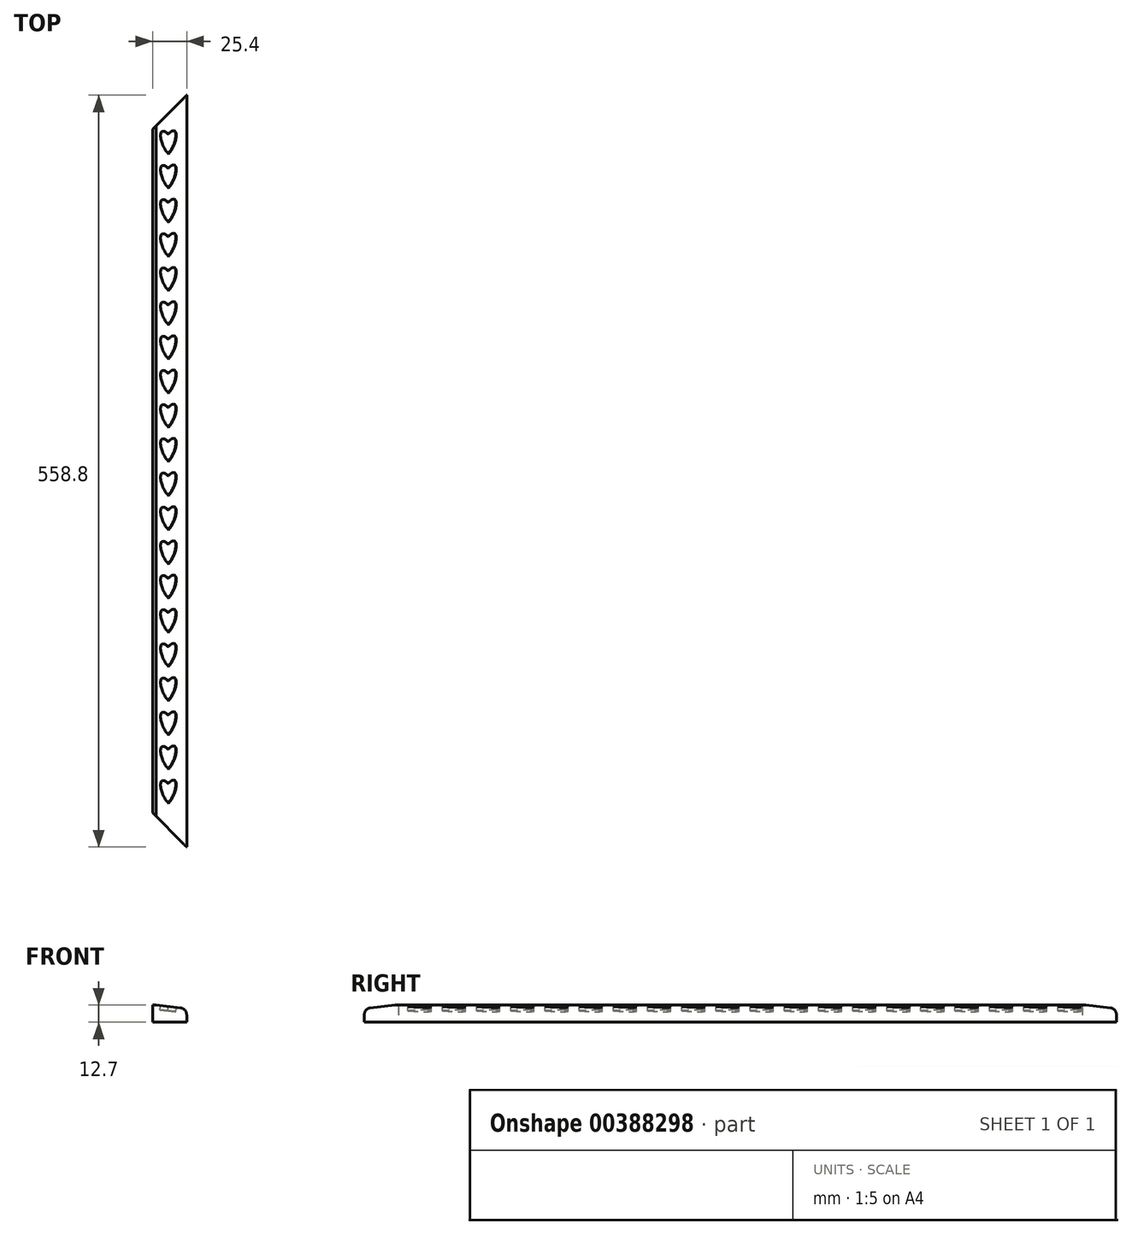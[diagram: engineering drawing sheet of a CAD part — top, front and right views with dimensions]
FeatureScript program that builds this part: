
annotation { "Feature Type Name" : "Feature", "Feature Type Description" : "" }
export const myFeature = defineFeature(function(context is Context, id is Id, definition is map)
    precondition{}
    {
        {
            var Q0;
            Q0=qCreatedBy(makeId("Top.planeOp"),FACE);
            var sketch = newSketch(context, id + "F0", { "sketchPlane" : qUnion([Q0])});
            skLineSegment(sketch, "E0.bottom", {"start": v(-12.7, 279.4) * mm, "end": v(12.7, 279.4) * mm});
            skLineSegment(sketch, "E0.top", {"start": v(-12.7, -279.4) * mm, "end": v(12.7, -279.4) * mm});
            skLineSegment(sketch, "E0.left", {"start": v(-12.7, 279.4) * mm, "end": v(-12.7, -279.4) * mm});
            skLineSegment(sketch, "E0.right", {"start": v(12.7, 279.4) * mm, "end": v(12.7, -279.4) * mm});
            skPoint(sketch, "E0.middle", {"position": v(0, 0) * mm});
            skPoint(sketch, "E1.end.orphan", {"position": v(12.7, -254) * mm});
            skPoint(sketch, "E2.MirrorCS.end.orphan", {"position": v(12.7, 254) * mm});
            skPoint(sketch, "E2.MirrorCS.start.orphan", {"position": v(-12.7, 279.4) * mm});
            skLineSegment(sketch, "E3", {"start": v(12.7, 279.4) * mm, "end": v(-12.7, 254) * mm});
            skLineSegment(sketch, "E4.MirrorCS", {"start": v(12.7, -279.4) * mm, "end": v(-12.7, -254) * mm});
            skSolve(sketch);
        }
        {
            var Q0;
            Q0=makeQuery(id+"F0.imprint","IMPRINT",FACE,{"disambiguationData":[TD([[makeQuery(id+"F0.imprint","IMPRINT",EDGE,{"derivedFrom":sQuery(id+"F0.wireOp",EDGE,"E0.right")}),-1.0]])]});
            extrude(context, id + "F1", {"entities" : qUnion([Q0]), "depth" : 12.7 * mm});
        }
        {
            var Q0;
            Q0=makeQuery(id+"F1.opExtrude","CAP_EDGE",EDGE,{"disambiguationData":[OSD([sQuery(id+"F0.wireOp",EDGE,"E0.right")])],"isStart":false});
            chamfer(context, id + "F2", {"entities" : qUnion([Q0]), "chamferType" : ChamferType.TWO_OFFSETS, "width1" : 2.54 * mm, "oppositeDirection" : false, "width2" : 22.86 * mm, "tangentPropagation" : true});
        }
        {
            var Q0;
            {var subQ0=sQuery(id+"F0.wireOp",EDGE,"E0.right");Q0=makeQuery(id+"F2.opChamfer","BLEND_EDGE",EDGE,{"blendedFrom":[makeQuery(id+"F1.opExtrude","CAP_EDGE",EDGE,{"disambiguationData":[OSD([subQ0])],"isStart":false}),makeQuery(id+"F1.opExtrude","SWEPT_FACE",FACE,{"disambiguationData":[OSD([subQ0])]})],"blendedInto":[makeQuery(id+"F1.opExtrude","SWEPT_FACE",FACE,{"disambiguationData":[OSD([subQ0])]})]});}
            fillet(context, id + "F3", {"entities" : qUnion([Q0]), "radius" : 5.08 * mm, "tangentPropagation" : true, "allowEdgeOverflow" : false});
        }
        {
            var Q0;
            Q0=makeQuery(id+"F2.opChamfer","BLEND_FACE",FACE,{"disambiguationData":[OSD([sQuery(id+"F0.wireOp",EDGE,"E0.right")])]});
            var sketch = newSketch(context, id + "F4", { "sketchPlane" : qUnion([Q0])});
            skLineSegment(sketch, "E5.bottom", {"start": v(-8.83, 253.3) * mm, "end": v(4.54, 253.3) * mm});
            skLineSegment(sketch, "E5.top", {"start": v(-8.83, 232.97) * mm, "end": v(4.54, 232.97) * mm});
            skLineSegment(sketch, "E5.left", {"start": v(-8.83, 253.3) * mm, "end": v(-8.83, 232.97) * mm});
            skLineSegment(sketch, "E5.right", {"start": v(4.54, 253.3) * mm, "end": v(4.54, 232.97) * mm});
            skEllipticalArc(sketch, "E6", {});
            skPoint(sketch, "E6.centerSnap0", {"position": v(-8.83, 243.13) * mm});
            skPoint(sketch, "E6.centerSnap1", {"position": v(-2.15, 232.97) * mm});
            skEllipticalArc(sketch, "E7", {});
            skLineSegment(sketch, "E8", {"start": v(-2.22, 250.5) * mm, "end": v(-1.95, 250.22) * mm});
            skPoint(sketch, "E9.left.start.orphan", {"position": v(-11.37, 255.83) * mm});
            skLineSegment(sketch, "E10.0.1.0", {"start": v(-8.83, 227.9) * mm, "end": v(4.54, 227.9) * mm});
            skPoint(sketch, "E10.0.1.1", {"position": v(-2.15, 207.57) * mm});
            skLineSegment(sketch, "E10.0.1.2", {"start": v(-8.83, 227.9) * mm, "end": v(-8.83, 207.57) * mm});
            skPoint(sketch, "E10.0.1.3", {"position": v(-11.37, 230.43) * mm});
            skLineSegment(sketch, "E10.0.1.4", {"start": v(4.54, 227.9) * mm, "end": v(4.54, 207.57) * mm});
            skPoint(sketch, "E10.0.1.5", {"position": v(-8.83, 217.73) * mm});
            skEllipticalArc(sketch, "E10.0.1.6", {});
            skEllipticalArc(sketch, "E10.0.1.7", {});
            skLineSegment(sketch, "E10.0.1.8", {"start": v(-8.83, 207.57) * mm, "end": v(4.54, 207.57) * mm});
            skLineSegment(sketch, "E10.0.1.9", {"start": v(-2.22, 225.1) * mm, "end": v(-1.95, 224.82) * mm});
            skLineSegment(sketch, "E10.0.2.0", {"start": v(-8.83, 202.5) * mm, "end": v(4.54, 202.5) * mm});
            skPoint(sketch, "E10.0.2.1", {"position": v(-2.15, 182.17) * mm});
            skLineSegment(sketch, "E10.0.2.2", {"start": v(-8.83, 202.5) * mm, "end": v(-8.83, 182.17) * mm});
            skPoint(sketch, "E10.0.2.3", {"position": v(-11.37, 205.03) * mm});
            skLineSegment(sketch, "E10.0.2.4", {"start": v(4.54, 202.5) * mm, "end": v(4.54, 182.17) * mm});
            skPoint(sketch, "E10.0.2.5", {"position": v(-8.83, 192.33) * mm});
            skEllipticalArc(sketch, "E10.0.2.6", {});
            skEllipticalArc(sketch, "E10.0.2.7", {});
            skLineSegment(sketch, "E10.0.2.8", {"start": v(-8.83, 182.17) * mm, "end": v(4.54, 182.17) * mm});
            skLineSegment(sketch, "E10.0.2.9", {"start": v(-2.22, 199.7) * mm, "end": v(-1.95, 199.42) * mm});
            skLineSegment(sketch, "E10.0.3.0", {"start": v(-8.83, 177.1) * mm, "end": v(4.54, 177.1) * mm});
            skPoint(sketch, "E10.0.3.1", {"position": v(-2.15, 156.77) * mm});
            skLineSegment(sketch, "E10.0.3.2", {"start": v(-8.83, 177.1) * mm, "end": v(-8.83, 156.77) * mm});
            skPoint(sketch, "E10.0.3.3", {"position": v(-11.37, 179.63) * mm});
            skLineSegment(sketch, "E10.0.3.4", {"start": v(4.54, 177.1) * mm, "end": v(4.54, 156.77) * mm});
            skPoint(sketch, "E10.0.3.5", {"position": v(-8.83, 166.93) * mm});
            skEllipticalArc(sketch, "E10.0.3.6", {});
            skEllipticalArc(sketch, "E10.0.3.7", {});
            skLineSegment(sketch, "E10.0.3.8", {"start": v(-8.83, 156.77) * mm, "end": v(4.54, 156.77) * mm});
            skLineSegment(sketch, "E10.0.3.9", {"start": v(-2.22, 174.3) * mm, "end": v(-1.95, 174.02) * mm});
            skLineSegment(sketch, "E10.0.4.0", {"start": v(-8.83, 151.7) * mm, "end": v(4.54, 151.7) * mm});
            skPoint(sketch, "E10.0.4.1", {"position": v(-2.15, 131.37) * mm});
            skLineSegment(sketch, "E10.0.4.2", {"start": v(-8.83, 151.7) * mm, "end": v(-8.83, 131.37) * mm});
            skPoint(sketch, "E10.0.4.3", {"position": v(-11.37, 154.23) * mm});
            skLineSegment(sketch, "E10.0.4.4", {"start": v(4.54, 151.7) * mm, "end": v(4.54, 131.37) * mm});
            skPoint(sketch, "E10.0.4.5", {"position": v(-8.83, 141.53) * mm});
            skEllipticalArc(sketch, "E10.0.4.6", {});
            skEllipticalArc(sketch, "E10.0.4.7", {});
            skLineSegment(sketch, "E10.0.4.8", {"start": v(-8.83, 131.37) * mm, "end": v(4.54, 131.37) * mm});
            skLineSegment(sketch, "E10.0.4.9", {"start": v(-2.22, 148.9) * mm, "end": v(-1.95, 148.62) * mm});
            skLineSegment(sketch, "E10.0.5.0", {"start": v(-8.83, 126.3) * mm, "end": v(4.54, 126.3) * mm});
            skPoint(sketch, "E10.0.5.1", {"position": v(-2.15, 105.97) * mm});
            skLineSegment(sketch, "E10.0.5.2", {"start": v(-8.83, 126.3) * mm, "end": v(-8.83, 105.97) * mm});
            skPoint(sketch, "E10.0.5.3", {"position": v(-11.37, 128.83) * mm});
            skLineSegment(sketch, "E10.0.5.4", {"start": v(4.54, 126.3) * mm, "end": v(4.54, 105.97) * mm});
            skPoint(sketch, "E10.0.5.5", {"position": v(-8.83, 116.13) * mm});
            skEllipticalArc(sketch, "E10.0.5.6", {});
            skEllipticalArc(sketch, "E10.0.5.7", {});
            skLineSegment(sketch, "E10.0.5.8", {"start": v(-8.83, 105.97) * mm, "end": v(4.54, 105.97) * mm});
            skLineSegment(sketch, "E10.0.5.9", {"start": v(-2.22, 123.5) * mm, "end": v(-1.95, 123.22) * mm});
            skLineSegment(sketch, "E10.0.6.0", {"start": v(-8.83, 100.9) * mm, "end": v(4.54, 100.9) * mm});
            skPoint(sketch, "E10.0.6.1", {"position": v(-2.15, 80.57) * mm});
            skLineSegment(sketch, "E10.0.6.2", {"start": v(-8.83, 100.9) * mm, "end": v(-8.83, 80.57) * mm});
            skPoint(sketch, "E10.0.6.3", {"position": v(-11.37, 103.43) * mm});
            skLineSegment(sketch, "E10.0.6.4", {"start": v(4.54, 100.9) * mm, "end": v(4.54, 80.57) * mm});
            skPoint(sketch, "E10.0.6.5", {"position": v(-8.83, 90.73) * mm});
            skEllipticalArc(sketch, "E10.0.6.6", {});
            skEllipticalArc(sketch, "E10.0.6.7", {});
            skLineSegment(sketch, "E10.0.6.8", {"start": v(-8.83, 80.57) * mm, "end": v(4.54, 80.57) * mm});
            skLineSegment(sketch, "E10.0.6.9", {"start": v(-2.22, 98.1) * mm, "end": v(-1.95, 97.82) * mm});
            skLineSegment(sketch, "E10.0.7.0", {"start": v(-8.83, 75.5) * mm, "end": v(4.54, 75.5) * mm});
            skPoint(sketch, "E10.0.7.1", {"position": v(-2.15, 55.17) * mm});
            skLineSegment(sketch, "E10.0.7.2", {"start": v(-8.83, 75.5) * mm, "end": v(-8.83, 55.17) * mm});
            skPoint(sketch, "E10.0.7.3", {"position": v(-11.37, 78.03) * mm});
            skLineSegment(sketch, "E10.0.7.4", {"start": v(4.54, 75.5) * mm, "end": v(4.54, 55.17) * mm});
            skPoint(sketch, "E10.0.7.5", {"position": v(-8.83, 65.33) * mm});
            skEllipticalArc(sketch, "E10.0.7.6", {});
            skEllipticalArc(sketch, "E10.0.7.7", {});
            skLineSegment(sketch, "E10.0.7.8", {"start": v(-8.83, 55.17) * mm, "end": v(4.54, 55.17) * mm});
            skLineSegment(sketch, "E10.0.7.9", {"start": v(-2.22, 72.7) * mm, "end": v(-1.95, 72.42) * mm});
            skLineSegment(sketch, "E10.0.8.0", {"start": v(-8.83, 50.1) * mm, "end": v(4.54, 50.1) * mm});
            skPoint(sketch, "E10.0.8.1", {"position": v(-2.15, 29.77) * mm});
            skLineSegment(sketch, "E10.0.8.2", {"start": v(-8.83, 50.1) * mm, "end": v(-8.83, 29.77) * mm});
            skPoint(sketch, "E10.0.8.3", {"position": v(-11.37, 52.63) * mm});
            skLineSegment(sketch, "E10.0.8.4", {"start": v(4.54, 50.1) * mm, "end": v(4.54, 29.77) * mm});
            skPoint(sketch, "E10.0.8.5", {"position": v(-8.83, 39.93) * mm});
            skEllipticalArc(sketch, "E10.0.8.6", {});
            skEllipticalArc(sketch, "E10.0.8.7", {});
            skLineSegment(sketch, "E10.0.8.8", {"start": v(-8.83, 29.77) * mm, "end": v(4.54, 29.77) * mm});
            skLineSegment(sketch, "E10.0.8.9", {"start": v(-2.22, 47.3) * mm, "end": v(-1.95, 47.02) * mm});
            skLineSegment(sketch, "E10.0.9.0", {"start": v(-8.83, 24.7) * mm, "end": v(4.54, 24.7) * mm});
            skPoint(sketch, "E10.0.9.1", {"position": v(-2.15, 4.37) * mm});
            skLineSegment(sketch, "E10.0.9.2", {"start": v(-8.83, 24.7) * mm, "end": v(-8.83, 4.37) * mm});
            skPoint(sketch, "E10.0.9.3", {"position": v(-11.37, 27.23) * mm});
            skLineSegment(sketch, "E10.0.9.4", {"start": v(4.54, 24.7) * mm, "end": v(4.54, 4.37) * mm});
            skPoint(sketch, "E10.0.9.5", {"position": v(-8.83, 14.53) * mm});
            skEllipticalArc(sketch, "E10.0.9.6", {});
            skEllipticalArc(sketch, "E10.0.9.7", {});
            skLineSegment(sketch, "E10.0.9.8", {"start": v(-8.83, 4.37) * mm, "end": v(4.54, 4.37) * mm});
            skLineSegment(sketch, "E10.0.9.9", {"start": v(-2.22, 21.9) * mm, "end": v(-1.95, 21.62) * mm});
            skLineSegment(sketch, "E10.0.10.0", {"start": v(-8.83, -0.7) * mm, "end": v(4.54, -0.7) * mm});
            skPoint(sketch, "E10.0.10.1", {"position": v(-2.15, -21.03) * mm});
            skLineSegment(sketch, "E10.0.10.2", {"start": v(-8.83, -0.7) * mm, "end": v(-8.83, -21.03) * mm});
            skPoint(sketch, "E10.0.10.3", {"position": v(-11.37, 1.83) * mm});
            skLineSegment(sketch, "E10.0.10.4", {"start": v(4.54, -0.7) * mm, "end": v(4.54, -21.03) * mm});
            skPoint(sketch, "E10.0.10.5", {"position": v(-8.83, -10.87) * mm});
            skEllipticalArc(sketch, "E10.0.10.6", {});
            skEllipticalArc(sketch, "E10.0.10.7", {});
            skLineSegment(sketch, "E10.0.10.8", {"start": v(-8.83, -21.03) * mm, "end": v(4.54, -21.03) * mm});
            skLineSegment(sketch, "E10.0.10.9", {"start": v(-2.22, -3.5) * mm, "end": v(-1.95, -3.78) * mm});
            skLineSegment(sketch, "E10.0.11.0", {"start": v(-8.83, -26.1) * mm, "end": v(4.54, -26.1) * mm});
            skPoint(sketch, "E10.0.11.1", {"position": v(-2.15, -46.43) * mm});
            skLineSegment(sketch, "E10.0.11.2", {"start": v(-8.83, -26.1) * mm, "end": v(-8.83, -46.43) * mm});
            skPoint(sketch, "E10.0.11.3", {"position": v(-11.37, -23.57) * mm});
            skLineSegment(sketch, "E10.0.11.4", {"start": v(4.54, -26.1) * mm, "end": v(4.54, -46.43) * mm});
            skPoint(sketch, "E10.0.11.5", {"position": v(-8.83, -36.27) * mm});
            skEllipticalArc(sketch, "E10.0.11.6", {});
            skEllipticalArc(sketch, "E10.0.11.7", {});
            skLineSegment(sketch, "E10.0.11.8", {"start": v(-8.83, -46.43) * mm, "end": v(4.54, -46.43) * mm});
            skLineSegment(sketch, "E10.0.11.9", {"start": v(-2.22, -28.9) * mm, "end": v(-1.95, -29.18) * mm});
            skLineSegment(sketch, "E10.0.12.0", {"start": v(-8.83, -51.5) * mm, "end": v(4.54, -51.5) * mm});
            skPoint(sketch, "E10.0.12.1", {"position": v(-2.15, -71.83) * mm});
            skLineSegment(sketch, "E10.0.12.2", {"start": v(-8.83, -51.5) * mm, "end": v(-8.83, -71.83) * mm});
            skPoint(sketch, "E10.0.12.3", {"position": v(-11.37, -48.97) * mm});
            skLineSegment(sketch, "E10.0.12.4", {"start": v(4.54, -51.5) * mm, "end": v(4.54, -71.83) * mm});
            skPoint(sketch, "E10.0.12.5", {"position": v(-8.83, -61.67) * mm});
            skEllipticalArc(sketch, "E10.0.12.6", {});
            skEllipticalArc(sketch, "E10.0.12.7", {});
            skLineSegment(sketch, "E10.0.12.8", {"start": v(-8.83, -71.83) * mm, "end": v(4.54, -71.83) * mm});
            skLineSegment(sketch, "E10.0.12.9", {"start": v(-2.22, -54.3) * mm, "end": v(-1.95, -54.58) * mm});
            skLineSegment(sketch, "E10.0.13.0", {"start": v(-8.83, -76.9) * mm, "end": v(4.54, -76.9) * mm});
            skPoint(sketch, "E10.0.13.1", {"position": v(-2.15, -97.23) * mm});
            skLineSegment(sketch, "E10.0.13.2", {"start": v(-8.83, -76.9) * mm, "end": v(-8.83, -97.23) * mm});
            skPoint(sketch, "E10.0.13.3", {"position": v(-11.37, -74.37) * mm});
            skLineSegment(sketch, "E10.0.13.4", {"start": v(4.54, -76.9) * mm, "end": v(4.54, -97.23) * mm});
            skPoint(sketch, "E10.0.13.5", {"position": v(-8.83, -87.07) * mm});
            skEllipticalArc(sketch, "E10.0.13.6", {});
            skEllipticalArc(sketch, "E10.0.13.7", {});
            skLineSegment(sketch, "E10.0.13.8", {"start": v(-8.83, -97.23) * mm, "end": v(4.54, -97.23) * mm});
            skLineSegment(sketch, "E10.0.13.9", {"start": v(-2.22, -79.7) * mm, "end": v(-1.95, -79.98) * mm});
            skLineSegment(sketch, "E10.0.14.0", {"start": v(-8.83, -102.3) * mm, "end": v(4.54, -102.3) * mm});
            skPoint(sketch, "E10.0.14.1", {"position": v(-2.15, -122.63) * mm});
            skLineSegment(sketch, "E10.0.14.2", {"start": v(-8.83, -102.3) * mm, "end": v(-8.83, -122.63) * mm});
            skPoint(sketch, "E10.0.14.3", {"position": v(-11.37, -99.77) * mm});
            skLineSegment(sketch, "E10.0.14.4", {"start": v(4.54, -102.3) * mm, "end": v(4.54, -122.63) * mm});
            skPoint(sketch, "E10.0.14.5", {"position": v(-8.83, -112.47) * mm});
            skEllipticalArc(sketch, "E10.0.14.6", {});
            skEllipticalArc(sketch, "E10.0.14.7", {});
            skLineSegment(sketch, "E10.0.14.8", {"start": v(-8.83, -122.63) * mm, "end": v(4.54, -122.63) * mm});
            skLineSegment(sketch, "E10.0.14.9", {"start": v(-2.22, -105.1) * mm, "end": v(-1.95, -105.38) * mm});
            skLineSegment(sketch, "E10.0.15.0", {"start": v(-8.83, -127.7) * mm, "end": v(4.54, -127.7) * mm});
            skPoint(sketch, "E10.0.15.1", {"position": v(-2.15, -148.03) * mm});
            skLineSegment(sketch, "E10.0.15.2", {"start": v(-8.83, -127.7) * mm, "end": v(-8.83, -148.03) * mm});
            skPoint(sketch, "E10.0.15.3", {"position": v(-11.37, -125.17) * mm});
            skLineSegment(sketch, "E10.0.15.4", {"start": v(4.54, -127.7) * mm, "end": v(4.54, -148.03) * mm});
            skPoint(sketch, "E10.0.15.5", {"position": v(-8.83, -137.87) * mm});
            skEllipticalArc(sketch, "E10.0.15.6", {});
            skEllipticalArc(sketch, "E10.0.15.7", {});
            skLineSegment(sketch, "E10.0.15.8", {"start": v(-8.83, -148.03) * mm, "end": v(4.54, -148.03) * mm});
            skLineSegment(sketch, "E10.0.15.9", {"start": v(-2.22, -130.5) * mm, "end": v(-1.95, -130.78) * mm});
            skLineSegment(sketch, "E10.0.16.0", {"start": v(-8.83, -153.1) * mm, "end": v(4.54, -153.1) * mm});
            skPoint(sketch, "E10.0.16.1", {"position": v(-2.15, -173.43) * mm});
            skLineSegment(sketch, "E10.0.16.2", {"start": v(-8.83, -153.1) * mm, "end": v(-8.83, -173.43) * mm});
            skPoint(sketch, "E10.0.16.3", {"position": v(-11.37, -150.57) * mm});
            skLineSegment(sketch, "E10.0.16.4", {"start": v(4.54, -153.1) * mm, "end": v(4.54, -173.43) * mm});
            skPoint(sketch, "E10.0.16.5", {"position": v(-8.83, -163.27) * mm});
            skEllipticalArc(sketch, "E10.0.16.6", {});
            skEllipticalArc(sketch, "E10.0.16.7", {});
            skLineSegment(sketch, "E10.0.16.8", {"start": v(-8.83, -173.43) * mm, "end": v(4.54, -173.43) * mm});
            skLineSegment(sketch, "E10.0.16.9", {"start": v(-2.22, -155.9) * mm, "end": v(-1.95, -156.18) * mm});
            skLineSegment(sketch, "E10.0.17.0", {"start": v(-8.83, -178.5) * mm, "end": v(4.54, -178.5) * mm});
            skPoint(sketch, "E10.0.17.1", {"position": v(-2.15, -198.83) * mm});
            skLineSegment(sketch, "E10.0.17.2", {"start": v(-8.83, -178.5) * mm, "end": v(-8.83, -198.83) * mm});
            skPoint(sketch, "E10.0.17.3", {"position": v(-11.37, -175.97) * mm});
            skLineSegment(sketch, "E10.0.17.4", {"start": v(4.54, -178.5) * mm, "end": v(4.54, -198.83) * mm});
            skPoint(sketch, "E10.0.17.5", {"position": v(-8.83, -188.67) * mm});
            skEllipticalArc(sketch, "E10.0.17.6", {});
            skEllipticalArc(sketch, "E10.0.17.7", {});
            skLineSegment(sketch, "E10.0.17.8", {"start": v(-8.83, -198.83) * mm, "end": v(4.54, -198.83) * mm});
            skLineSegment(sketch, "E10.0.17.9", {"start": v(-2.22, -181.3) * mm, "end": v(-1.95, -181.58) * mm});
            skLineSegment(sketch, "E10.direction1", {"start": v(-8.83, 232.97) * mm, "end": v(16.57, 232.97) * mm, "construction": true});
            skLineSegment(sketch, "E10.direction2", {"start": v(-8.83, 232.97) * mm, "end": v(-8.83, 207.57) * mm, "construction": true});
            skLineSegment(sketch, "E11.0.1.0", {"start": v(-8.83, -224.23) * mm, "end": v(4.54, -224.23) * mm});
            skPoint(sketch, "E11.0.1.1", {"position": v(-2.15, -224.23) * mm});
            skPoint(sketch, "E11.0.1.3", {"position": v(-11.37, -201.37) * mm});
            skPoint(sketch, "E11.0.1.4", {"position": v(-8.83, -214.07) * mm});
            skLineSegment(sketch, "E11.0.1.5", {"start": v(-8.83, -203.9) * mm, "end": v(4.54, -203.9) * mm});
            skLineSegment(sketch, "E11.0.1.6", {"start": v(-8.83, -203.9) * mm, "end": v(-8.83, -224.23) * mm});
            skLineSegment(sketch, "E11.0.1.7", {"start": v(4.54, -203.9) * mm, "end": v(4.54, -224.23) * mm});
            skEllipticalArc(sketch, "E11.0.1.8", {});
            skEllipticalArc(sketch, "E11.0.1.9", {});
            skLineSegment(sketch, "E11.0.1.10", {"start": v(-2.22, -206.7) * mm, "end": v(-1.95, -206.98) * mm});
            skLineSegment(sketch, "E11.0.2.0", {"start": v(-8.83, -249.63) * mm, "end": v(4.54, -249.63) * mm});
            skPoint(sketch, "E11.0.2.1", {"position": v(-2.15, -249.63) * mm});
            skPoint(sketch, "E11.0.2.2", {"position": v(-2.15, -224.23) * mm});
            skPoint(sketch, "E11.0.2.3", {"position": v(-11.37, -226.77) * mm});
            skPoint(sketch, "E11.0.2.4", {"position": v(-8.83, -239.47) * mm});
            skLineSegment(sketch, "E11.0.2.5", {"start": v(-8.83, -229.3) * mm, "end": v(4.54, -229.3) * mm});
            skLineSegment(sketch, "E11.0.2.6", {"start": v(-8.83, -229.3) * mm, "end": v(-8.83, -249.63) * mm});
            skLineSegment(sketch, "E11.0.2.7", {"start": v(4.54, -229.3) * mm, "end": v(4.54, -249.63) * mm});
            skEllipticalArc(sketch, "E11.0.2.8", {});
            skEllipticalArc(sketch, "E11.0.2.9", {});
            skLineSegment(sketch, "E11.0.2.10", {"start": v(-2.22, -232.1) * mm, "end": v(-1.95, -232.38) * mm});
            skLineSegment(sketch, "E11.direction1", {"start": v(-8.83, -198.83) * mm, "end": v(16.57, -198.83) * mm, "construction": true});
            skLineSegment(sketch, "E11.direction2", {"start": v(-8.83, -198.83) * mm, "end": v(-8.83, -224.23) * mm, "construction": true});
            const initialGuessF4  = {"E6": [-0.0021461910774663966, 0.24313098626136784, -0.44549528212436185, 0.8952842864727022, 0.0104013, 0.0041656, 5.4030752140367095, 2.2614825604469164], "E7": [-0.0021461910774663966, 0.24313098626136784, 0.42639124113221455, 0.9045388380195346, 0.0106934, 0.004089400000000001, 4.043989840250925, 0.9023971866611309], "E10.0.1.6": [-0.0021461910774663966, 0.21773098626136783, 0.42639124113221455, 0.9045388380195346, 0.0106934, 0.004089400000000001, 4.043989840250925, 0.9023971866611308], "E10.0.1.7": [-0.0021461910774663966, 0.21773098626136783, -0.44549528212436185, 0.8952842864727022, 0.0104013, 0.0041656, 5.4030752140367095, 2.2614825604469164], "E10.0.2.6": [-0.0021461910774663966, 0.19233098626136783, 0.42639124113221455, 0.9045388380195346, 0.0106934, 0.004089400000000001, 4.043989840250925, 0.9023971866611308], "E10.0.2.7": [-0.0021461910774663966, 0.19233098626136783, -0.44549528212436185, 0.8952842864727022, 0.0104013, 0.0041656, 5.4030752140367095, 2.2614825604469164], "E10.0.3.6": [-0.0021461910774663966, 0.16693098626136782, 0.42639124113221455, 0.9045388380195346, 0.0106934, 0.004089400000000001, 4.043989840250925, 0.9023971866611308], "E10.0.3.7": [-0.0021461910774663966, 0.16693098626136782, -0.44549528212436185, 0.8952842864727022, 0.0104013, 0.0041656, 5.4030752140367095, 2.2614825604469164], "E10.0.4.6": [-0.0021461910774663966, 0.1415309862613678, 0.42639124113221455, 0.9045388380195346, 0.0106934, 0.004089400000000001, 4.043989840250925, 0.9023971866611308], "E10.0.4.7": [-0.0021461910774663966, 0.1415309862613678, -0.44549528212436185, 0.8952842864727022, 0.0104013, 0.0041656, 5.4030752140367095, 2.2614825604469164], "E10.0.5.6": [-0.0021461910774663966, 0.11613098626136781, 0.42639124113221455, 0.9045388380195346, 0.0106934, 0.004089400000000001, 4.043989840250925, 0.9023971866611308], "E10.0.5.7": [-0.0021461910774663966, 0.11613098626136781, -0.44549528212436185, 0.8952842864727022, 0.0104013, 0.0041656, 5.4030752140367095, 2.2614825604469164], "E10.0.6.6": [-0.0021461910774663966, 0.0907309862613678, 0.42639124113221455, 0.9045388380195346, 0.0106934, 0.004089400000000001, 4.043989840250925, 0.9023971866611308], "E10.0.6.7": [-0.0021461910774663966, 0.0907309862613678, -0.44549528212436185, 0.8952842864727022, 0.0104013, 0.0041656, 5.4030752140367095, 2.2614825604469164], "E10.0.7.6": [-0.0021461910774663966, 0.0653309862613678, 0.42639124113221455, 0.9045388380195346, 0.0106934, 0.004089400000000001, 4.043989840250925, 0.9023971866611308], "E10.0.7.7": [-0.0021461910774663966, 0.0653309862613678, -0.44549528212436185, 0.8952842864727022, 0.0104013, 0.0041656, 5.4030752140367095, 2.2614825604469164], "E10.0.8.6": [-0.0021461910774663966, 0.03993098626136779, 0.42639124113221455, 0.9045388380195346, 0.0106934, 0.004089400000000001, 4.043989840250925, 0.9023971866611308], "E10.0.8.7": [-0.0021461910774663966, 0.03993098626136779, -0.44549528212436185, 0.8952842864727022, 0.0104013, 0.0041656, 5.4030752140367095, 2.261482560446917], "E10.0.9.6": [-0.0021461910774663966, 0.014530986261367784, 0.42639124113221455, 0.9045388380195346, 0.0106934, 0.004089400000000001, 4.043989840250925, 0.9023971866611308], "E10.0.9.7": [-0.0021461910774663966, 0.014530986261367784, -0.44549528212436185, 0.8952842864727022, 0.0104013, 0.0041656, 5.4030752140367095, 2.2614825604469164], "E10.0.10.6": [-0.0021461910774663966, -0.010869013738632222, 0.42639124113221455, 0.9045388380195346, 0.0106934, 0.004089400000000001, 4.043989840250925, 0.9023971866611308], "E10.0.10.7": [-0.0021461910774663966, -0.010869013738632222, -0.44549528212436185, 0.8952842864727022, 0.0104013, 0.0041656, 5.4030752140367095, 2.2614825604469164], "E10.0.11.6": [-0.0021461910774663966, -0.036269013738632255, 0.42639124113221455, 0.9045388380195346, 0.0106934, 0.004089400000000001, 4.043989840250925, 0.9023971866611308], "E10.0.11.7": [-0.0021461910774663966, -0.036269013738632255, -0.44549528212436185, 0.8952842864727022, 0.0104013, 0.0041656, 5.4030752140367095, 2.2614825604469164], "E10.0.12.6": [-0.0021461910774663966, -0.06166901373863223, 0.42639124113221455, 0.9045388380195346, 0.0106934, 0.004089400000000001, 4.043989840250925, 0.9023971866611308], "E10.0.12.7": [-0.0021461910774663966, -0.06166901373863223, -0.44549528212436185, 0.8952842864727022, 0.0104013, 0.0041656, 5.4030752140367095, 2.2614825604469164], "E10.0.13.6": [-0.0021461910774663966, -0.08706901373863221, 0.42639124113221455, 0.9045388380195346, 0.0106934, 0.004089400000000001, 4.043989840250925, 0.9023971866611308], "E10.0.13.7": [-0.0021461910774663966, -0.08706901373863221, -0.44549528212436185, 0.8952842864727022, 0.0104013, 0.0041656, 5.4030752140367095, 2.2614825604469164], "E10.0.14.6": [-0.0021461910774663966, -0.11246901373863225, 0.42639124113221455, 0.9045388380195346, 0.0106934, 0.004089400000000001, 4.043989840250925, 0.9023971866611308], "E10.0.14.7": [-0.0021461910774663966, -0.11246901373863225, -0.44549528212436185, 0.8952842864727022, 0.0104013, 0.0041656, 5.4030752140367095, 2.2614825604469164], "E10.0.15.6": [-0.0021461910774663966, -0.13786901373863228, 0.42639124113221455, 0.9045388380195346, 0.0106934, 0.004089400000000001, 4.043989840250925, 0.9023971866611308], "E10.0.15.7": [-0.0021461910774663966, -0.13786901373863228, -0.44549528212436185, 0.8952842864727022, 0.0104013, 0.0041656, 5.4030752140367095, 2.2614825604469164], "E10.0.16.6": [-0.0021461910774663966, -0.16326901373863226, 0.42639124113221455, 0.9045388380195346, 0.0106934, 0.004089400000000001, 4.043989840250925, 0.9023971866611308], "E10.0.16.7": [-0.0021461910774663966, -0.16326901373863226, -0.44549528212436185, 0.8952842864727022, 0.0104013, 0.0041656, 5.4030752140367095, 2.2614825604469164], "E10.0.17.6": [-0.0021461910774663966, -0.18866901373863224, 0.42639124113221455, 0.9045388380195346, 0.0106934, 0.004089400000000001, 4.043989840250925, 0.9023971866611308], "E10.0.17.7": [-0.0021461910774663966, -0.18866901373863224, -0.44549528212436185, 0.8952842864727022, 0.0104013, 0.0041656, 5.4030752140367095, 2.2614825604469164], "E11.0.1.8": [-0.0021461910774663966, -0.21406901373863224, 0.42639124113221455, 0.9045388380195346, 0.0106934, 0.004089400000000001, 4.043989840250925, 0.9023971866611307], "E11.0.1.9": [-0.0021461910774663966, -0.21406901373863224, -0.44549528212436185, 0.8952842864727022, 0.0104013, 0.0041656, 5.4030752140367095, 2.2614825604469164], "E11.0.2.8": [-0.0021461910774663966, -0.23946901373863225, 0.42639124113221455, 0.9045388380195346, 0.0106934, 0.004089400000000001, 4.043989840250925, 0.9023971866611307], "E11.0.2.9": [-0.0021461910774663966, -0.23946901373863225, -0.44549528212436185, 0.8952842864727022, 0.0104013, 0.0041656, 5.4030752140367095, 2.2614825604469164]};
            skSetInitialGuess(sketch, initialGuessF4);
            skSolve(sketch);
        }
        {
            var Q0;
            Q0=makeQuery(id+"F4.imprint","IMPRINT",FACE,{"disambiguationData":[TD([[makeQuery(id+"F4.imprint","IMPRINT",EDGE,{"derivedFrom":sQuery(id+"F4.wireOp",EDGE,"E6")}),1.0]])]});
            var Q1;
            Q1=makeQuery(id+"F4.imprint","IMPRINT",FACE,{"disambiguationData":[TD([[makeQuery(id+"F4.imprint","IMPRINT",EDGE,{"derivedFrom":sQuery(id+"F4.wireOp",EDGE,"E10.0.1.6")}),1.0]])]});
            var Q2;
            Q2=makeQuery(id+"F4.imprint","IMPRINT",FACE,{"disambiguationData":[TD([[makeQuery(id+"F4.imprint","IMPRINT",EDGE,{"derivedFrom":sQuery(id+"F4.wireOp",EDGE,"E10.0.2.6")}),1.0]])]});
            var Q3;
            Q3=makeQuery(id+"F4.imprint","IMPRINT",FACE,{"disambiguationData":[TD([[makeQuery(id+"F4.imprint","IMPRINT",EDGE,{"derivedFrom":sQuery(id+"F4.wireOp",EDGE,"E10.0.3.6")}),1.0]])]});
            var Q4;
            Q4=makeQuery(id+"F4.imprint","IMPRINT",FACE,{"disambiguationData":[TD([[makeQuery(id+"F4.imprint","IMPRINT",EDGE,{"derivedFrom":sQuery(id+"F4.wireOp",EDGE,"E10.0.4.6")}),1.0]])]});
            var Q5;
            Q5=makeQuery(id+"F4.imprint","IMPRINT",FACE,{"disambiguationData":[TD([[makeQuery(id+"F4.imprint","IMPRINT",EDGE,{"derivedFrom":sQuery(id+"F4.wireOp",EDGE,"E10.0.5.6")}),1.0]])]});
            var Q6;
            Q6=makeQuery(id+"F4.imprint","IMPRINT",FACE,{"disambiguationData":[TD([[makeQuery(id+"F4.imprint","IMPRINT",EDGE,{"derivedFrom":sQuery(id+"F4.wireOp",EDGE,"E10.0.6.6")}),1.0]])]});
            var Q7;
            Q7=makeQuery(id+"F4.imprint","IMPRINT",FACE,{"disambiguationData":[TD([[makeQuery(id+"F4.imprint","IMPRINT",EDGE,{"derivedFrom":sQuery(id+"F4.wireOp",EDGE,"E10.0.7.6")}),1.0]])]});
            var Q8;
            Q8=makeQuery(id+"F4.imprint","IMPRINT",FACE,{"disambiguationData":[TD([[makeQuery(id+"F4.imprint","IMPRINT",EDGE,{"derivedFrom":sQuery(id+"F4.wireOp",EDGE,"E10.0.8.6")}),1.0]])]});
            var Q9;
            Q9=makeQuery(id+"F4.imprint","IMPRINT",FACE,{"disambiguationData":[TD([[makeQuery(id+"F4.imprint","IMPRINT",EDGE,{"derivedFrom":sQuery(id+"F4.wireOp",EDGE,"E10.0.9.6")}),1.0]])]});
            var Q10;
            Q10=makeQuery(id+"F4.imprint","IMPRINT",FACE,{"disambiguationData":[TD([[makeQuery(id+"F4.imprint","IMPRINT",EDGE,{"derivedFrom":sQuery(id+"F4.wireOp",EDGE,"E10.0.10.6")}),1.0]])]});
            var Q11;
            Q11=makeQuery(id+"F4.imprint","IMPRINT",FACE,{"disambiguationData":[TD([[makeQuery(id+"F4.imprint","IMPRINT",EDGE,{"derivedFrom":sQuery(id+"F4.wireOp",EDGE,"E10.0.11.6")}),1.0]])]});
            var Q12;
            Q12=makeQuery(id+"F4.imprint","IMPRINT",FACE,{"disambiguationData":[TD([[makeQuery(id+"F4.imprint","IMPRINT",EDGE,{"derivedFrom":sQuery(id+"F4.wireOp",EDGE,"E10.0.12.6")}),1.0]])]});
            var Q13;
            Q13=makeQuery(id+"F4.imprint","IMPRINT",FACE,{"disambiguationData":[TD([[makeQuery(id+"F4.imprint","IMPRINT",EDGE,{"derivedFrom":sQuery(id+"F4.wireOp",EDGE,"E10.0.13.6")}),1.0]])]});
            var Q14;
            Q14=makeQuery(id+"F4.imprint","IMPRINT",FACE,{"disambiguationData":[TD([[makeQuery(id+"F4.imprint","IMPRINT",EDGE,{"derivedFrom":sQuery(id+"F4.wireOp",EDGE,"E10.0.14.6")}),1.0]])]});
            var Q15;
            Q15=makeQuery(id+"F4.imprint","IMPRINT",FACE,{"disambiguationData":[TD([[makeQuery(id+"F4.imprint","IMPRINT",EDGE,{"derivedFrom":sQuery(id+"F4.wireOp",EDGE,"E10.0.15.6")}),1.0]])]});
            var Q16;
            Q16=makeQuery(id+"F4.imprint","IMPRINT",FACE,{"disambiguationData":[TD([[makeQuery(id+"F4.imprint","IMPRINT",EDGE,{"derivedFrom":sQuery(id+"F4.wireOp",EDGE,"E10.0.16.6")}),1.0]])]});
            var Q17;
            Q17=makeQuery(id+"F4.imprint","IMPRINT",FACE,{"disambiguationData":[TD([[makeQuery(id+"F4.imprint","IMPRINT",EDGE,{"derivedFrom":sQuery(id+"F4.wireOp",EDGE,"E10.0.17.6")}),1.0]])]});
            var Q18;
            Q18=makeQuery(id+"F4.imprint","IMPRINT",FACE,{"disambiguationData":[TD([[makeQuery(id+"F4.imprint","IMPRINT",EDGE,{"derivedFrom":sQuery(id+"F4.wireOp",EDGE,"E11.0.1.8")}),1.0]])]});
            var Q19;
            Q19=makeQuery(id+"F4.imprint","IMPRINT",FACE,{"disambiguationData":[TD([[makeQuery(id+"F4.imprint","IMPRINT",EDGE,{"derivedFrom":sQuery(id+"F4.wireOp",EDGE,"E11.0.2.8")}),1.0]])]});
            extrude(context, id + "F5", {"entities" : qUnion([Q0, Q1, Q2, Q3, Q4, Q5, Q6, Q7, Q8, Q9, Q10, Q11, Q12, Q13, Q14, Q15, Q16, Q17, Q18, Q19]), "operationType" : NewBodyOperationType.REMOVE, "oppositeDirection" : true, "depth" : 3.17 * mm});
        }
    });
